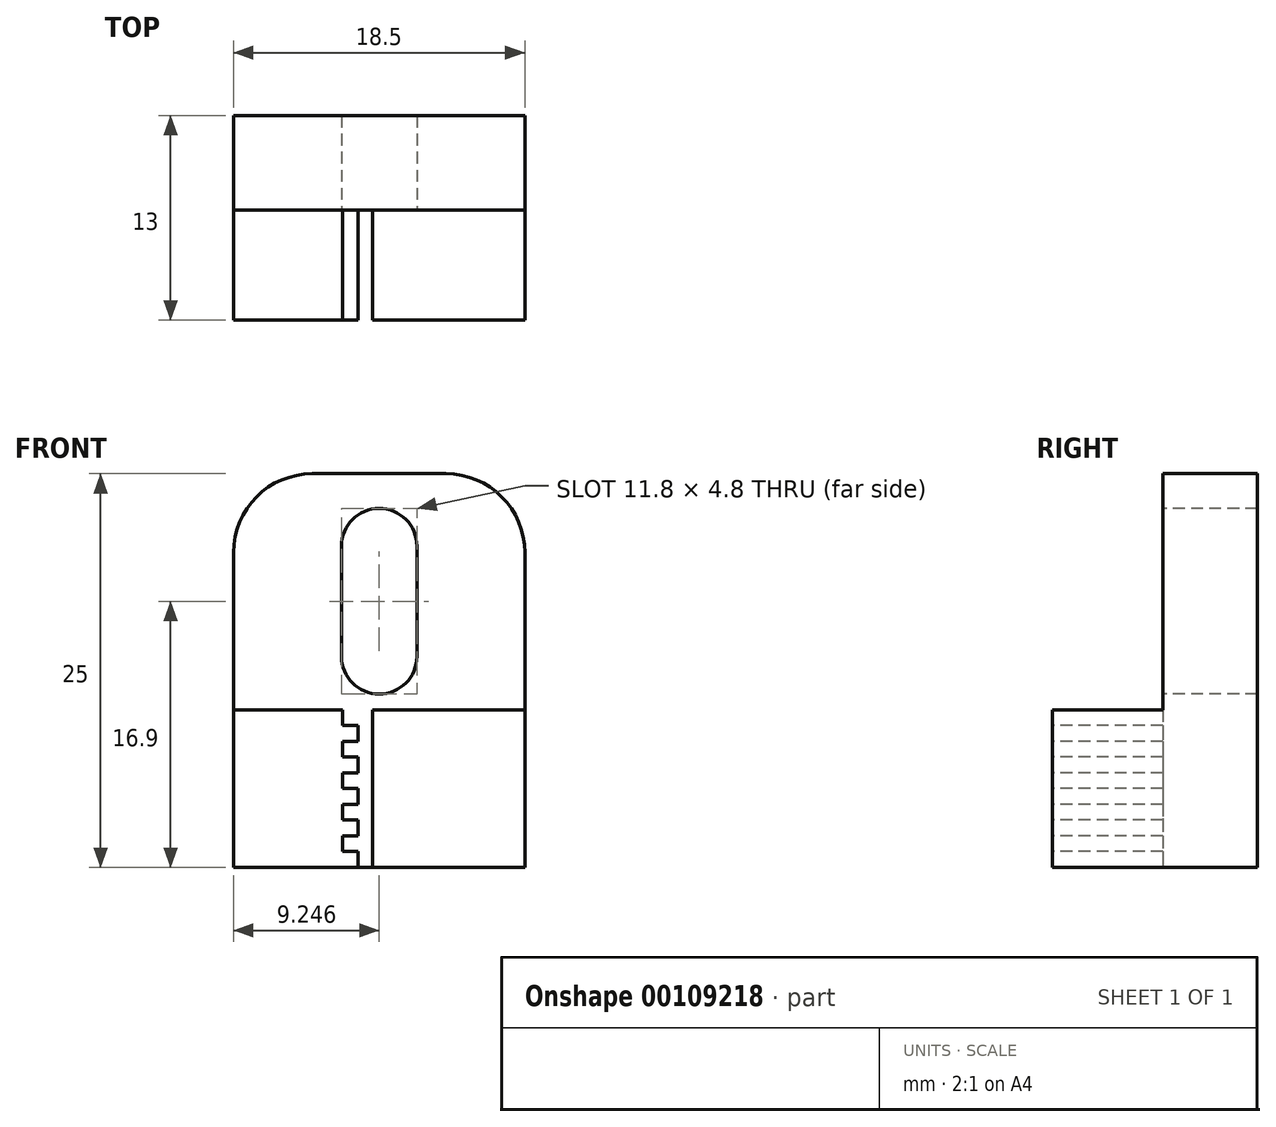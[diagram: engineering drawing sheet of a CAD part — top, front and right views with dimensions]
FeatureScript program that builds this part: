
annotation { "Feature Type Name" : "Feature", "Feature Type Description" : "" }
export const myFeature = defineFeature(function(context is Context, id is Id, definition is map)
    precondition{}
    {
        {
            var Q0;
            Q0=qCreatedBy(makeId("Top.planeOp"),FACE);
            var sketch = newSketch(context, id + "F0", { "sketchPlane" : qUnion([Q0])});
            skLineSegment(sketch, "E0.bottom", {"start": v(-4.96, 0) * mm, "end": v(13.54, 0) * mm});
            skLineSegment(sketch, "E0.top", {"start": v(-4.96, 25) * mm, "end": v(13.54, 25) * mm});
            skLineSegment(sketch, "E0.left", {"start": v(-4.96, 0) * mm, "end": v(-4.96, 25) * mm});
            skLineSegment(sketch, "E0.right", {"start": v(13.54, 0) * mm, "end": v(13.54, 25) * mm});
            skLineSegment(sketch, "E1", {"start": v(-4.96, 5) * mm, "end": v(13.54, 5) * mm});
            skLineSegment(sketch, "E2.bottom", {"start": v(-4.96, 17.95) * mm, "end": v(-1.96, 17.95) * mm});
            skLineSegment(sketch, "E2.top", {"start": v(-4.96, 12.05) * mm, "end": v(-1.96, 12.05) * mm});
            skLineSegment(sketch, "E2.left", {"start": v(-4.96, 17.95) * mm, "end": v(-4.96, 12.05) * mm});
            skLineSegment(sketch, "E2.right", {"start": v(-1.96, 17.95) * mm, "end": v(-1.96, 12.05) * mm});
            skLineSegment(sketch, "E3.bottom", {"start": v(13.54, 17.95) * mm, "end": v(10.54, 17.95) * mm});
            skLineSegment(sketch, "E3.top", {"start": v(13.54, 12.05) * mm, "end": v(10.54, 12.05) * mm});
            skLineSegment(sketch, "E3.left", {"start": v(13.54, 17.95) * mm, "end": v(13.54, 12.05) * mm});
            skLineSegment(sketch, "E3.right", {"start": v(10.54, 17.95) * mm, "end": v(10.54, 12.05) * mm});
            skPoint(sketch, "E4", {"position": v(-1.96, 15) * mm});
            skPoint(sketch, "E5", {"position": v(-4.96, 15) * mm});
            skLineSegment(sketch, "E6", {"start": v(-4.96, 15) * mm, "end": v(13.54, 15) * mm});
            skLineSegment(sketch, "E7", {"start": v(-4.96, 13) * mm, "end": v(13.54, 13) * mm});
            skSolve(sketch);
        }
        {
            var Q0;
            {var subQ0=sQuery(id+"F0.wireOp",EDGE,"E0.bottom");Q0=makeQuery(id+"F0.imprint","IMPRINT",FACE,{"disambiguationData":[TD([[makeQuery(id+"F0.imprint","IMPRINT",EDGE,{"derivedFrom":subQ0}),1.0]])]});}
            var Q1;
            {var subQ0=sQuery(id+"F0.wireOp",EDGE,"E1");Q1=makeQuery(id+"F0.imprint","IMPRINT",FACE,{"disambiguationData":[TD([[makeQuery(id+"F0.imprint","IMPRINT",EDGE,{"derivedFrom":subQ0}),1.0]])]});}
            var Q2;
            {var subQ0=sQuery(id+"F0.wireOp",EDGE,"E2.top");Q2=makeQuery(id+"F0.imprint","IMPRINT",FACE,{"disambiguationData":[TD([[makeQuery(id+"F0.imprint","IMPRINT",EDGE,{"derivedFrom":subQ0}),1.0]])]});}
            var Q3;
            {var subQ0=sQuery(id+"F0.wireOp",EDGE,"E3.top");Q3=makeQuery(id+"F0.imprint","IMPRINT",FACE,{"disambiguationData":[TD([[makeQuery(id+"F0.imprint","IMPRINT",EDGE,{"derivedFrom":subQ0}),-1.0]])]});}
            extrude(context, id + "F1", {"entities" : qUnion([Q0, Q1, Q2, Q3]), "depth" : 10 * mm});
        }
        {
            var Q0;
            Q0=makeQuery(id+"F1.opExtrude","SWEPT_FACE",FACE,{"disambiguationData":[OSD([sQuery(id+"F0.wireOp",EDGE,"E0.bottom")])]});
            var sketch = newSketch(context, id + "F2", { "sketchPlane" : qUnion([Q0])});
            skLineSegment(sketch, "E8", {"start": v(1.96, 10) * mm, "end": v(1.96, 9) * mm});
            skLineSegment(sketch, "E9", {"start": v(1.96, 9) * mm, "end": v(2.96, 9) * mm});
            skLineSegment(sketch, "E10", {"start": v(2.96, 9) * mm, "end": v(2.96, 8) * mm});
            skLineSegment(sketch, "E11", {"start": v(2.96, 8) * mm, "end": v(1.96, 8) * mm});
            skLineSegment(sketch, "E12", {"start": v(1.96, 8) * mm, "end": v(1.96, 7) * mm});
            skLineSegment(sketch, "E13", {"start": v(1.96, 7) * mm, "end": v(2.96, 7) * mm});
            skLineSegment(sketch, "E14", {"start": v(2.96, 7) * mm, "end": v(2.96, 6) * mm});
            skLineSegment(sketch, "E15", {"start": v(2.96, 6) * mm, "end": v(1.96, 6) * mm});
            skLineSegment(sketch, "E16", {"start": v(1.96, 6) * mm, "end": v(1.96, 5) * mm});
            skLineSegment(sketch, "E17", {"start": v(1.96, 5) * mm, "end": v(2.96, 5) * mm});
            skLineSegment(sketch, "E18", {"start": v(2.96, 5) * mm, "end": v(2.96, 4) * mm});
            skLineSegment(sketch, "E19", {"start": v(2.96, 4) * mm, "end": v(1.96, 4) * mm});
            skLineSegment(sketch, "E20", {"start": v(1.96, 4) * mm, "end": v(1.96, 3) * mm});
            skLineSegment(sketch, "E21", {"start": v(1.96, 3) * mm, "end": v(2.96, 3) * mm});
            skLineSegment(sketch, "E22", {"start": v(2.96, 3) * mm, "end": v(2.96, 2) * mm});
            skLineSegment(sketch, "E23", {"start": v(2.96, 2) * mm, "end": v(1.96, 2) * mm});
            skLineSegment(sketch, "E24", {"start": v(1.96, 2) * mm, "end": v(1.96, 1) * mm});
            skLineSegment(sketch, "E25", {"start": v(1.96, 1) * mm, "end": v(2.96, 1) * mm});
            skLineSegment(sketch, "E26", {"start": v(2.96, 1) * mm, "end": v(2.96, 0) * mm});
            skLineSegment(sketch, "E27", {"start": v(2.96, 0) * mm, "end": v(1.96, 0) * mm});
            skLineSegment(sketch, "E28", {"start": v(3.86, 10) * mm, "end": v(3.86, 0) * mm});
            skLineSegment(sketch, "E29", {"start": v(1.96, 10) * mm, "end": v(3.86, 10) * mm});
            skLineSegment(sketch, "E30", {"start": v(3.86, 0) * mm, "end": v(2.96, 0) * mm});
            skSolve(sketch);
        }
        {
            var Q0;
            Q0=makeQuery(id+"F2.imprint","IMPRINT",FACE,{"disambiguationData":[TD([[makeQuery(id+"F2.imprint","IMPRINT",EDGE,{"derivedFrom":sQuery(id+"F2.wireOp",EDGE,"E8")}),1.0]])]});
            extrude(context, id + "F3", {"entities" : qUnion([Q0]), "operationType" : NewBodyOperationType.REMOVE, "oppositeDirection" : true, "depth" : 7 * mm});
        }
        {
            var Q0;
            Q0=makeQuery(id+"F1.opExtrude","CAP_FACE",FACE,{"disambiguationData":[OSD([sQuery(id+"F0.wireOp",EDGE,"E0.bottom"),sQuery(id+"F0.wireOp",EDGE,"E0.left"),sQuery(id+"F0.wireOp",EDGE,"E0.right"),sQuery(id+"F0.wireOp",EDGE,"E7")])],"isStart":false});
            var sketch = newSketch(context, id + "F4", { "sketchPlane" : qUnion([Q0])});
            skLineSegment(sketch, "E31.bottom", {"start": v(-4.96, 0) * mm, "end": v(13.54, 0) * mm});
            skLineSegment(sketch, "E31.top", {"start": v(-4.96, 7) * mm, "end": v(13.54, 7) * mm});
            skLineSegment(sketch, "E31.left", {"start": v(-4.96, 7) * mm, "end": v(-4.96, 0) * mm});
            skLineSegment(sketch, "E31.right", {"start": v(13.54, 7) * mm, "end": v(13.54, 0) * mm});
            skSolve(sketch);
        }
        {
            var Q0;
            {var subQ0=makeQuery(id+"F1.opExtrude","CAP_EDGE",EDGE,{"disambiguationData":[OSD([sQuery(id+"F0.wireOp",EDGE,"E7")])],"isStart":false});Q0=makeQuery(id+"F4.imprint","IMPRINT",FACE,{"disambiguationData":[TD([[makeQuery(id+"F4.imprint","IMPRINT",EDGE,{"derivedFrom":subQ0}),-1.0]])]});}
            extrude(context, id + "F5", {"entities" : qUnion([Q0]), "operationType" : NewBodyOperationType.ADD, "depth" : 15 * mm});
        }
        {
            var Q0;
            Q0=makeQuery(id+"F5.boolean.opBoolean","MERGE",FACE,{"derivedFrom":[makeQuery(id+"F3.boolean.opBoolean","COPY",FACE,{"derivedFrom":makeQuery(id+"F3.opExtrude","CAP_FACE",FACE,{"disambiguationData":[OSD([sQuery(id+"F2.wireOp",EDGE,"E8"),sQuery(id+"F2.wireOp",EDGE,"E9"),sQuery(id+"F2.wireOp",EDGE,"E10"),sQuery(id+"F2.wireOp",EDGE,"E11"),sQuery(id+"F2.wireOp",EDGE,"E12"),sQuery(id+"F2.wireOp",EDGE,"E13"),sQuery(id+"F2.wireOp",EDGE,"E14"),sQuery(id+"F2.wireOp",EDGE,"E15"),sQuery(id+"F2.wireOp",EDGE,"E16"),sQuery(id+"F2.wireOp",EDGE,"E17"),sQuery(id+"F2.wireOp",EDGE,"E18"),sQuery(id+"F2.wireOp",EDGE,"E19"),sQuery(id+"F2.wireOp",EDGE,"E20"),sQuery(id+"F2.wireOp",EDGE,"E21"),sQuery(id+"F2.wireOp",EDGE,"E22"),sQuery(id+"F2.wireOp",EDGE,"E23"),sQuery(id+"F2.wireOp",EDGE,"E24"),sQuery(id+"F2.wireOp",EDGE,"E25"),sQuery(id+"F2.wireOp",EDGE,"E26"),sQuery(id+"F2.wireOp",EDGE,"E28"),sQuery(id+"F2.wireOp",EDGE,"E29"),sQuery(id+"F2.wireOp",EDGE,"E30")])],"isStart":false})}),makeQuery(id+"F5.opExtrude","SWEPT_FACE",FACE,{"disambiguationData":[OSD([sQuery(id+"F4.wireOp",EDGE,"E31.top")])]})]});
            var sketch = newSketch(context, id + "F6", { "sketchPlane" : qUnion([Q0])});
            skArc(sketch, "E32", {"start": v(6.69, 20.4) * mm, "mid": v(4.29, 22.8) * mm, "end": v(1.89, 20.4) * mm});
            skArc(sketch, "E33", {"start": v(1.89, 13.4) * mm, "mid": v(4.29, 11) * mm, "end": v(6.69, 13.4) * mm});
            skLineSegment(sketch, "E34", {"start": v(1.89, 20.4) * mm, "end": v(1.89, 13.4) * mm});
            skLineSegment(sketch, "E35", {"start": v(6.69, 20.4) * mm, "end": v(6.69, 13.4) * mm});
            skPoint(sketch, "E36", {"position": v(4.29, 25) * mm});
            skLineSegment(sketch, "E37", {"start": v(4.29, 10) * mm, "end": v(4.29, 11) * mm});
            skLineSegment(sketch, "E38", {"start": v(4.29, 22.8) * mm, "end": v(4.29, 25) * mm});
            skSolve(sketch);
        }
        {
            var Q0;
            Q0=qSketchRegion(id+"F6",true);
            extrude(context, id + "F7", {"entities" : qUnion([Q0]), "operationType" : NewBodyOperationType.REMOVE, "oppositeDirection" : true, "depth" : 25 * mm});
        }
        {
            var Q0;
            Q0=makeQuery(id+"F5.opExtrude","CAP_EDGE",EDGE,{"disambiguationData":[OSD([sQuery(id+"F0.wireOp",EDGE,"E0.left"),sQuery(id+"F0.wireOp",EDGE,"E2.left")])],"isStart":false});
            var Q1;
            Q1=makeQuery(id+"F5.opExtrude","CAP_EDGE",EDGE,{"disambiguationData":[OSD([sQuery(id+"F0.wireOp",EDGE,"E0.right"),sQuery(id+"F0.wireOp",EDGE,"E3.left")])],"isStart":false});
            fillet(context, id + "F8", {"entities" : qUnion([Q0, Q1]), "radius" : 5 * mm, "tangentPropagation" : true, "allowEdgeOverflow" : false});
        }
    });
